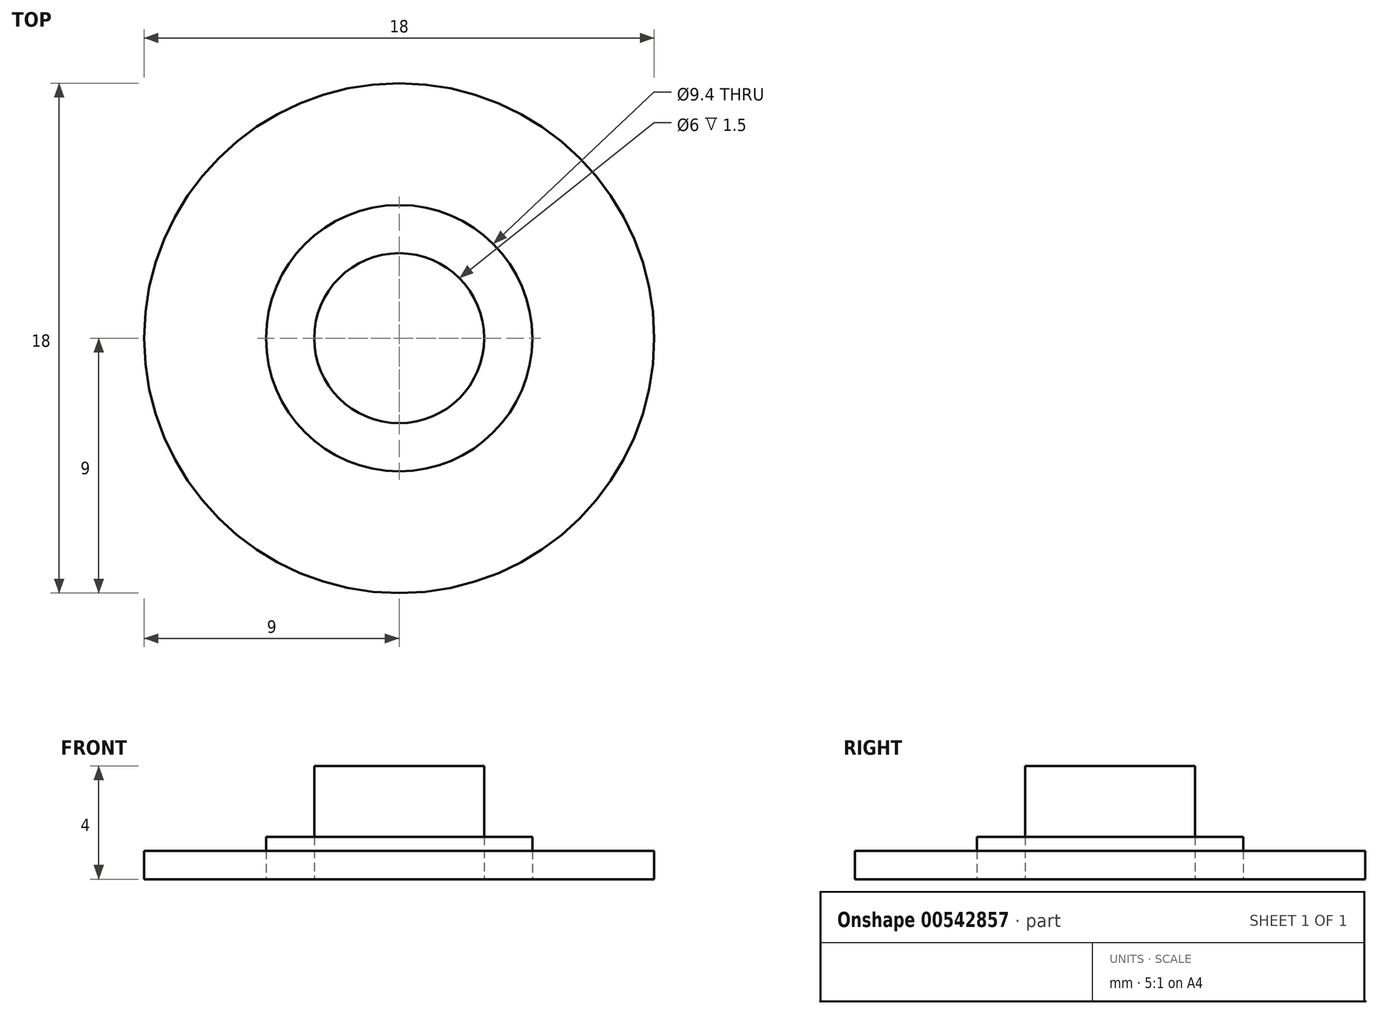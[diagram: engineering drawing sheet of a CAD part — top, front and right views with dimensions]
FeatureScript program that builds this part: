
annotation { "Feature Type Name" : "Feature", "Feature Type Description" : "" }
export const myFeature = defineFeature(function(context is Context, id is Id, definition is map)
    precondition{}
    {
        {
            var Q0;
            Q0=qCreatedBy(makeId("Top.planeOp"),FACE);
            var sketch = newSketch(context, id + "F0", { "sketchPlane" : qUnion([Q0])});
            skCircle(sketch, "E0", {"center": v(0, 0) * mm, "radius": 9 * mm});
            skCircle(sketch, "E1", {"center": v(0, 0) * mm, "radius": 3 * mm});
            skCircle(sketch, "E2", {"center": v(0, 0) * mm, "radius": 4.7 * mm});
            skSolve(sketch);
        }
        {
            var Q0;
            Q0=makeQuery(id+"F0.imprint","IMPRINT",FACE,{"disambiguationData":[TD([[makeQuery(id+"F0.imprint","IMPRINT",EDGE,{"derivedFrom":sQuery(id+"F0.wireOp",EDGE,"E1")}),1.0]])]});
            extrude(context, id + "F1", {"entities" : qUnion([Q0]), "depth" : 4 * mm, "offsetDistance" : 25 * mm});
        }
        {
            var Q0;
            Q0 = qSketchRegion(id + "F0", true);
            extrude(context, id + "F2", {"entities" : qUnion([Q0]), "operationType" : NewBodyOperationType.ADD, "depth" : 1 * mm, "offsetDistance" : 25 * mm});
        }
        {
            var Q0;
            Q0=makeQuery(id+"F0.imprint","IMPRINT",FACE,{"disambiguationData":[TD([[makeQuery(id+"F0.imprint","IMPRINT",EDGE,{"derivedFrom":sQuery(id+"F0.wireOp",EDGE,"E1")}),-1.0]])]});
            extrude(context, id + "F3", {"entities" : qUnion([Q0]), "depth" : 1.5 * mm, "offsetDistance" : 25 * mm});
        }
    });
